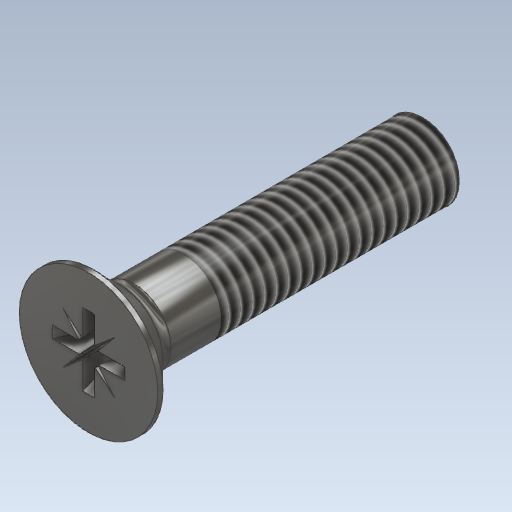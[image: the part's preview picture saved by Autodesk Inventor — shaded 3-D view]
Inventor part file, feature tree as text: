
AUTODESK INVENTOR PART (.ipt)
format: ipt  version: 2020 (Build 240168000, 168)  size: 290,816 bytes
history: mixed  units: mm
features: other x2, thread x1, imported_body x1
ambient origin geometry x8: Origin, YZ Plane, XZ Plane, XY Plane, X Axis, Y Axis, Z Axis, Center Point
bodies: Body1 (imported_parasolid)
feature tree (4):
  other  "Sólido1"
  thread  "Rosca1"  [1 undecoded]
  other  "Cut-Loft1"
  imported_body  NMx_Import_Brep_tag  [imported B-rep: ~10 faces, bbox_mm=[0.480761, 0.0, 20.380761]]
note: 1 required parameter value undecoded (feature->parameter linkage not recoverable at this tier; creation-order binding heuristic only, values carry confidence <= 0.55)
